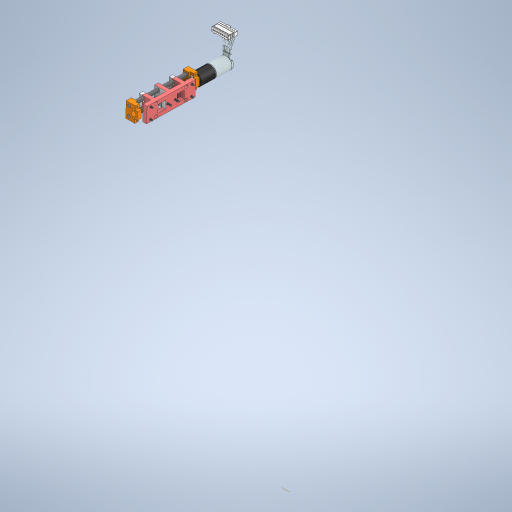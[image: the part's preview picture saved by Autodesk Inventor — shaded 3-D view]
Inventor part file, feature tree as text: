
AUTODESK INVENTOR PART (.ipt)
format: ipt  version: 2023 (Build 270158000, 158)  size: 9,598,464 bytes
history: native  units: mm
features: other x40, sketch x1
ambient origin geometry x8: Origin, YZ Plane, XZ Plane, XY Plane, X Axis, Y Axis, Z Axis, Center Point
bodies: Solid1 (feature_tree)
feature tree (41):
  other  "DifferentialLinearActuator.iam"
  other  "Part1.ipt:1"
  other  "GP16A_2-Stufig-110322.ipt:2"
  other  "283825_ec-max16_5w.ipt:2"
  other  "4145N198_Set Screw Precision Flexible Shaft Couplings.ipt:2"
  other  "91292A832_18-8 Stainless Steel Socket Head Screw.ipt:5"
  other  "91292A832_18-8 Stainless Steel Socket Head Screw.ipt:6"
  other  "MotorMountDifferential.ipt:1"
  other  "91828A113_18-8 Stainless Steel Hex Nut.ipt:1"
  other  "94450A564_Left-Hand Threaded 18-8 Stainless Steel Thin Hex Nut.ipt:3"
  other  "MotorDifferentialMountingBracket.ipt:1"
  other  "POMSliderMotorM25.ipt:1"
  other  "SliderFixtureM25.ipt:1"
  other  "POMSliderMotor.ipt:3"
  other  "POMSliderMotor.ipt:4"
  other  "91292A832_18-8 Stainless Steel Socket Head Screw.ipt:9"
  other  "91292A832_18-8 Stainless Steel Socket Head Screw.ipt:10"
  other  "91292A832_18-8 Stainless Steel Socket Head Screw.ipt:11"
  other  "91292A832_18-8 Stainless Steel Socket Head Screw.ipt:12"
  other  "91292A832_18-8 Stainless Steel Socket Head Screw.ipt:13"
  other  "91292A832_18-8 Stainless Steel Socket Head Screw.ipt:14"
  other  "91292A832_18-8 Stainless Steel Socket Head Screw.ipt:15"
  other  "91292A832_18-8 Stainless Steel Socket Head Screw.ipt:16"
  other  "91292A832_18-8 Stainless Steel Socket Head Screw.ipt:17"
  other  "91292A832_18-8 Stainless Steel Socket Head Screw.ipt:18"
  other  "AxisLinear.ipt:1"
  other  "AxisLinear.ipt:2"
  other  "91292A832_18-8 Stainless Steel Socket Head Screw.ipt:19"
  other  "91292A832_18-8 Stainless Steel Socket Head Screw.ipt:20"
  other  "MotorMountDifferential.ipt:2"
  other  "91292A832_18-8 Stainless Steel Socket Head Screw.ipt:21"
  other  "91292A832_18-8 Stainless Steel Socket Head Screw.ipt:22"
  other  "POMSliderAxis.ipt:1"
  other  "POMSliderAxis.ipt:2"
  other  "POMSliderAxis.ipt:3"
  other  "91292A832_18-8 Stainless Steel Socket Head Screw.ipt:23"
  other  "91292A832_18-8 Stainless Steel Socket Head Screw.ipt:24"
  other  "91292A832_18-8 Stainless Steel Socket Head Screw.ipt:25"
  other  "Screw.ipt:1"
  other  "Work Axis1"
  sketch  "Sketch6"  dims[d0=10.0mm]
